FCSTD DOCUMENT  (FreeCAD 0.16RUnknown)
Label: 2d-box
License: All rights reserved
LicenseURL: http://en.wikipedia.org/wiki/All_rights_reserved
objects: Sketcher::SketchObject×6, Spreadsheet::Sheet×1
note: 6 computed .brp shape members not serialized (recipe doc carries the construction recipe); baked Part::Feature solids carry a one-line shape summary decoded from their .brp

FEATURE [Spreadsheet::Sheet] Spreadsheet  label="prefs"
  cells = A1=width; B1(width)=100; C1=mm; A2=depth; B2(depth)=50; C2=mm; A3=height; B3(height)=30; C3=mm; A4=thickness; B4(thickness)=3; C4=mm; A5=space; B5(space)=2; C5=mm
FEATURE [Sketcher::SketchObject] Sketch  label="bottom"
  expr: Constraints[50] = prefs.width - 2 * prefs.thickness
  expr: Constraints[51] = prefs.width
  expr: Constraints[21] = prefs.depth - 2 * prefs.thickness
  expr: Constraints[20] = prefs.depth - 2 * prefs.thickness
  expr: Constraints[22] = prefs.depth
  sketch-geometry (21):
    g0: LineSegment StartX=3 StartY=47 StartZ=0 EndX=34.3333 EndY=47 EndZ=0
    g1: LineSegment StartX=34.3333 StartY=47 StartZ=0 EndX=34.3333 EndY=50 EndZ=0
    g2: LineSegment StartX=34.3333 StartY=50 StartZ=0 EndX=65.6667 EndY=50 EndZ=0
    g3: LineSegment StartX=65.6667 StartY=50 StartZ=0 EndX=65.6667 EndY=47 EndZ=0
    g4: LineSegment StartX=65.6667 StartY=47 StartZ=0 EndX=97 EndY=47 EndZ=0
    g5: LineSegment StartX=97 StartY=47 StartZ=0 EndX=97 EndY=32.3333 EndZ=0
    g6: LineSegment StartX=97 StartY=32.3333 StartZ=0 EndX=100 EndY=32.3333 EndZ=0
    g7: LineSegment StartX=100 StartY=32.3333 StartZ=0 EndX=100 EndY=17.6667 EndZ=0
    g8: LineSegment StartX=100 StartY=17.6667 StartZ=0 EndX=97 EndY=17.6667 EndZ=0
    g9: LineSegment StartX=97 StartY=17.6667 StartZ=0 EndX=97 EndY=3 EndZ=0
    g10: LineSegment StartX=97 StartY=3 StartZ=0 EndX=65.6667 EndY=3 EndZ=0
    g11: LineSegment StartX=65.6667 StartY=3 StartZ=0 EndX=65.6667 EndY=0 EndZ=0
    g12: LineSegment StartX=65.6667 StartY=0 StartZ=0 EndX=34.3333 EndY=0 EndZ=0
    g13: LineSegment StartX=34.3333 StartY=0 StartZ=0 EndX=34.3333 EndY=3 EndZ=0
    g14: LineSegment StartX=34.3333 StartY=3 StartZ=0 EndX=2.99998 EndY=3 EndZ=0
    g15: LineSegment StartX=2.99998 StartY=3 StartZ=0 EndX=2.99998 EndY=17.6667 EndZ=0
    g16: LineSegment StartX=2.99998 StartY=17.6667 StartZ=0 EndX=8.10663e-07 EndY=17.6667 EndZ=0
    g17: LineSegment StartX=8.10663e-07 StartY=17.6667 StartZ=0 EndX=8.10663e-07 EndY=32.3333 EndZ=0
    g18: LineSegment StartX=8.10663e-07 StartY=32.3333 StartZ=0 EndX=3 EndY=32.3333 EndZ=0
    g19: LineSegment StartX=3 StartY=32.3333 StartZ=0 EndX=3 EndY=47 EndZ=0
    g20: GeomPoint [constr] X=-41.8758 Y=-31.3252 Z=0
  constraints (60):
    c: Coincident(g0,g1)
    c: Coincident(g1,g2)
    c: Coincident(g2,g3)
    c: Coincident(g3,g4)
    c: Coincident(g4,g5)
    c: Coincident(g5,g6)
    c: Coincident(g6,g7)
    c: Coincident(g7,g8)
    c: Coincident(g8,g9)
    c: Coincident(g9,g10)
    c: Coincident(g10,g11)
    c: Coincident(g11,g12)
    c: Coincident(g12,g13)
    c: Coincident(g13,g14)
    c: Coincident(g14,g15)
    c: Coincident(g15,g16)
    c: Coincident(g16,g17)
    c: Coincident(g17,g18)
    c: Coincident(g18,g19)
    c: Coincident(g19,g0)
    c: DistanceY(g9,g4) = 44
    c: DistanceY(g14,g0) = 44
    c: DistanceY(g12,g1) = 50
    c: Horizontal(g0)
    c: Horizontal(g2)
    c: Horizontal(g4)
    c: Horizontal(g10)
    c: Horizontal(g12)
    c: Horizontal(g14)
    c: Equal(g1,g13)
    c: Equal(g0,g2)
    c: Equal(g2,g4)
    c: Equal(g4,g10)
    c: Equal(g10,g12)
    c: Equal(g12,g14)
    c: Equal(g3,g11)
    c: Equal(g5,g7)
    c: Equal(g7,g9)
    c: Equal(g9,g19)
    c: Equal(g19,g17)
    c: Equal(g17,g15)
    c: Vertical(g3)
    c: Vertical(g1)
    c: Vertical(g13)
    c: Vertical(g11)
    c: Horizontal(g18)
    c: Horizontal(g16)
    c: Horizontal(g8)
    c: Equal(g18,g6)
    c: Equal(g16,g8)
    c: DistanceX(g0,g4) = 94
    c: DistanceX(g16,g7) = 100
    c: Vertical(g15)
    c: Vertical(g19)
    c: Vertical(g17)
    c: Vertical(g5)
    c: Vertical(g7)
    c: Vertical(g9)
    c: DistanceX(g-1,g16) = 0
    c: DistanceY(g12,g-1) = 0
FEATURE [Sketcher::SketchObject] Sketch001  label="front"
  Placement = pos=(0,52,0) rot=(0,0,1;0rad)
  expr: Placement.Base.y = prefs.depth + prefs.space
  expr: Constraints[20] = prefs.height
  expr: Constraints[21] = prefs.height
  expr: Constraints[48] = prefs.width - 2 * prefs.thickness
  expr: Constraints[49] = prefs.width
  expr: Constraints[22] = prefs.height - 2 * prefs.thickness
  sketch-geometry (21):
    g0: LineSegment StartX=3 StartY=30 StartZ=0 EndX=34.3333 EndY=30 EndZ=0
    g1: LineSegment StartX=34.3333 StartY=30 StartZ=0 EndX=34.3333 EndY=27 EndZ=0
    g2: LineSegment StartX=34.3333 StartY=27 StartZ=0 EndX=65.6667 EndY=27 EndZ=0
    g3: LineSegment StartX=65.6667 StartY=27 StartZ=0 EndX=65.6667 EndY=30 EndZ=0
    g4: LineSegment StartX=65.6667 StartY=30 StartZ=0 EndX=97 EndY=30 EndZ=0
    g5: LineSegment StartX=97 StartY=30 StartZ=0 EndX=97 EndY=20 EndZ=0
    g6: LineSegment StartX=97 StartY=20 StartZ=0 EndX=100 EndY=20 EndZ=0
    g7: LineSegment StartX=100 StartY=20 StartZ=0 EndX=100 EndY=10 EndZ=0
    g8: LineSegment StartX=100 StartY=10 StartZ=0 EndX=97 EndY=10 EndZ=0
    g9: LineSegment StartX=97 StartY=10 StartZ=0 EndX=97 EndY=0 EndZ=0
    g10: LineSegment StartX=97 StartY=0 StartZ=0 EndX=65.6667 EndY=0 EndZ=0
    g11: LineSegment StartX=65.6667 StartY=0 StartZ=0 EndX=65.6667 EndY=3 EndZ=0
    g12: LineSegment StartX=65.6667 StartY=3 StartZ=0 EndX=34.3333 EndY=3 EndZ=0
    g13: LineSegment StartX=34.3333 StartY=3 StartZ=0 EndX=34.3333 EndY=0 EndZ=0
    g14: LineSegment StartX=34.3333 StartY=0 StartZ=0 EndX=2.99998 EndY=0 EndZ=0
    g15: LineSegment StartX=2.99998 StartY=0 StartZ=0 EndX=2.99998 EndY=10 EndZ=0
    g16: LineSegment StartX=2.99998 StartY=10 StartZ=0 EndX=8.10663e-07 EndY=10 EndZ=0
    g17: LineSegment StartX=8.10663e-07 StartY=10 StartZ=0 EndX=8.10663e-07 EndY=20 EndZ=0
    g18: LineSegment StartX=8.10663e-07 StartY=20 StartZ=0 EndX=3 EndY=20 EndZ=0
    g19: LineSegment StartX=3 StartY=20 StartZ=0 EndX=3 EndY=30 EndZ=0
    g20: GeomPoint [constr] X=-41.8758 Y=-31.3252 Z=0
  constraints (60):
    c: Coincident(g0,g1)
    c: Coincident(g1,g2)
    c: Coincident(g2,g3)
    c: Coincident(g3,g4)
    c: Coincident(g4,g5)
    c: Coincident(g5,g6)
    c: Coincident(g6,g7)
    c: Coincident(g7,g8)
    c: Coincident(g8,g9)
    c: Coincident(g9,g10)
    c: Coincident(g10,g11)
    c: Coincident(g11,g12)
    c: Coincident(g12,g13)
    c: Coincident(g13,g14)
    c: Coincident(g14,g15)
    c: Coincident(g15,g16)
    c: Coincident(g16,g17)
    c: Coincident(g17,g18)
    c: Coincident(g18,g19)
    c: Coincident(g19,g0)
    c: DistanceY(g9,g4) = 30
    c: DistanceY(g14,g0) = 30
    c: DistanceY(g12,g1) = 24
    c: Horizontal(g0)
    c: Horizontal(g2)
    c: Horizontal(g4)
    c: Horizontal(g10)
    c: Horizontal(g12)
    c: Horizontal(g14)
    c: Equal(g0,g2)
    c: Equal(g2,g4)
    c: Equal(g4,g10)
    c: Equal(g10,g12)
    c: Equal(g12,g14)
    c: Equal(g5,g7)
    c: Equal(g7,g9)
    c: Equal(g9,g19)
    c: Equal(g19,g17)
    c: Equal(g17,g15)
    c: Vertical(g3)
    c: Vertical(g1)
    c: Vertical(g13)
    c: Vertical(g11)
    c: Horizontal(g18)
    c: Horizontal(g16)
    c: Horizontal(g8)
    c: Equal(g18,g6)
    c: Equal(g16,g8)
    c: DistanceX(g0,g4) = 94
    c: DistanceX(g16,g7) = 100
    c: Vertical(g15)
    c: Vertical(g19)
    c: Vertical(g17)
    c: Vertical(g5)
    c: Vertical(g7)
    c: Vertical(g9)
    c: DistanceX(g-1,g16) = 0
    c: Equal(g1,g13)
    c: Equal(g3,g11)
    c: DistanceY(g-1,g14) = 0
FEATURE [Sketcher::SketchObject] Sketch002  label="left"
  Placement = pos=(0,84,0) rot=(0,0,1;0rad)
  expr: Constraints[59] = (prefs.depth - 2 * prefs.thickness) / 3
  expr: Constraints[53] = prefs.depth - 2 * prefs.thickness
  expr: Placement.Base.y = prefs.depth + prefs.height + prefs.space * 2
  expr: Constraints[20] = prefs.height
  expr: Constraints[21] = prefs.height
  expr: Constraints[54] = prefs.depth
  expr: Constraints[22] = prefs.height - 2 * prefs.thickness
  sketch-geometry (21):
    g0: LineSegment StartX=0 StartY=30 StartZ=0 EndX=17.6667 EndY=30 EndZ=0
    g1: LineSegment StartX=17.6667 StartY=30 StartZ=0 EndX=17.6667 EndY=27 EndZ=0
    g2: LineSegment StartX=17.6667 StartY=27 StartZ=0 EndX=32.3333 EndY=27 EndZ=0
    g3: LineSegment StartX=32.3333 StartY=27 StartZ=0 EndX=32.3333 EndY=30 EndZ=0
    g4: LineSegment StartX=32.3333 StartY=30 StartZ=0 EndX=50 EndY=30 EndZ=0
    g5: LineSegment StartX=50 StartY=30 StartZ=0 EndX=50 EndY=20 EndZ=0
    g6: LineSegment StartX=50 StartY=20 StartZ=0 EndX=47 EndY=20 EndZ=0
    g7: LineSegment StartX=47 StartY=20 StartZ=0 EndX=47 EndY=10 EndZ=0
    g8: LineSegment StartX=47 StartY=10 StartZ=0 EndX=50 EndY=10 EndZ=0
    g9: LineSegment StartX=50 StartY=10 StartZ=0 EndX=50 EndY=0 EndZ=0
    g10: LineSegment StartX=50 StartY=0 StartZ=0 EndX=32.3333 EndY=0 EndZ=0
    g11: LineSegment StartX=32.3333 StartY=0 StartZ=0 EndX=32.3333 EndY=3 EndZ=0
    g12: LineSegment StartX=32.3333 StartY=3 StartZ=0 EndX=17.6667 EndY=3 EndZ=0
    g13: LineSegment StartX=17.6667 StartY=3 StartZ=0 EndX=17.6667 EndY=0 EndZ=0
    g14: LineSegment StartX=17.6667 StartY=0 StartZ=0 EndX=0 EndY=0 EndZ=0
    g15: LineSegment StartX=0 StartY=0 StartZ=0 EndX=0 EndY=10 EndZ=0
    g16: LineSegment StartX=0 StartY=10 StartZ=0 EndX=3 EndY=10 EndZ=0
    g17: LineSegment StartX=3 StartY=10 StartZ=0 EndX=3 EndY=20 EndZ=0
    g18: LineSegment StartX=3 StartY=20 StartZ=0 EndX=0 EndY=20 EndZ=0
    g19: LineSegment StartX=0 StartY=20 StartZ=0 EndX=0 EndY=30 EndZ=0
    g20: GeomPoint [constr] X=-41.8758 Y=-31.3252 Z=0
  constraints (60):
    c: Coincident(g0,g1)
    c: Coincident(g1,g2)
    c: Coincident(g2,g3)
    c: Coincident(g3,g4)
    c: Coincident(g4,g5)
    c: Coincident(g5,g6)
    c: Coincident(g6,g7)
    c: Coincident(g7,g8)
    c: Coincident(g8,g9)
    c: Coincident(g9,g10)
    c: Coincident(g10,g11)
    c: Coincident(g11,g12)
    c: Coincident(g12,g13)
    c: Coincident(g13,g14)
    c: Coincident(g14,g15)
    c: Coincident(g15,g16)
    c: Coincident(g16,g17)
    c: Coincident(g17,g18)
    c: Coincident(g18,g19)
    c: Coincident(g19,g0)
    c: DistanceY(g9,g4) = 30
    c: DistanceY(g14,g0) = 30
    c: DistanceY(g12,g1) = 24
    c: Horizontal(g0)
    c: Horizontal(g2)
    c: Horizontal(g4)
    c: Horizontal(g10)
    c: Horizontal(g12)
    c: Horizontal(g14)
    c: Equal(g4,g10)
    c: Equal(g5,g7)
    c: Equal(g7,g9)
    c: Equal(g9,g19)
    c: Equal(g19,g17)
    c: Equal(g17,g15)
    c: Vertical(g3)
    c: Vertical(g1)
    c: Vertical(g13)
    c: Vertical(g11)
    c: Horizontal(g18)
    c: Horizontal(g16)
    c: Vertical(g15)
    c: Vertical(g19)
    c: Vertical(g17)
    c: Vertical(g5)
    c: Vertical(g7)
    c: Vertical(g9)
    c: Equal(g1,g13)
    c: Equal(g3,g11)
    c: DistanceY(g-1,g14) = 0
    c: Horizontal(g6)
    c: Equal(g18,g6)
    c: Equal(g16,g8)
    c: DistanceX(g17,g6) = 44
    c: DistanceX(g0,g4) = 50
    c: DistanceX(g-1,g14) = 0
    c: Equal(g14,g10)
    c: Equal(g0,g4)
    c: Equal(g2,g12)
    c: DistanceX(g2,g2) = 14.6667
FEATURE [Sketcher::SketchObject] Sketch003  label="top"
  Placement = pos=(102,0,0) rot=(0,0,1;0rad)
  expr: Placement.Base.x = prefs.width + prefs.space
  expr: Constraints[50] = prefs.width - 2 * prefs.thickness
  expr: Constraints[51] = prefs.width
  expr: Constraints[21] = prefs.depth - 2 * prefs.thickness
  expr: Constraints[20] = prefs.depth - 2 * prefs.thickness
  expr: Constraints[22] = prefs.depth
  sketch-geometry (21):
    g0: LineSegment StartX=3 StartY=47 StartZ=0 EndX=34.3333 EndY=47 EndZ=0
    g1: LineSegment StartX=34.3333 StartY=47 StartZ=0 EndX=34.3333 EndY=50 EndZ=0
    g2: LineSegment StartX=34.3333 StartY=50 StartZ=0 EndX=65.6667 EndY=50 EndZ=0
    g3: LineSegment StartX=65.6667 StartY=50 StartZ=0 EndX=65.6667 EndY=47 EndZ=0
    g4: LineSegment StartX=65.6667 StartY=47 StartZ=0 EndX=97 EndY=47 EndZ=0
    g5: LineSegment StartX=97 StartY=47 StartZ=0 EndX=97 EndY=32.3333 EndZ=0
    g6: LineSegment StartX=97 StartY=32.3333 StartZ=0 EndX=100 EndY=32.3333 EndZ=0
    g7: LineSegment StartX=100 StartY=32.3333 StartZ=0 EndX=100 EndY=17.6667 EndZ=0
    g8: LineSegment StartX=100 StartY=17.6667 StartZ=0 EndX=97 EndY=17.6667 EndZ=0
    g9: LineSegment StartX=97 StartY=17.6667 StartZ=0 EndX=97 EndY=3 EndZ=0
    g10: LineSegment StartX=97 StartY=3 StartZ=0 EndX=65.6667 EndY=3 EndZ=0
    g11: LineSegment StartX=65.6667 StartY=3 StartZ=0 EndX=65.6667 EndY=0 EndZ=0
    g12: LineSegment StartX=65.6667 StartY=0 StartZ=0 EndX=34.3333 EndY=0 EndZ=0
    g13: LineSegment StartX=34.3333 StartY=0 StartZ=0 EndX=34.3333 EndY=3 EndZ=0
    g14: LineSegment StartX=34.3333 StartY=3 StartZ=0 EndX=2.99998 EndY=3 EndZ=0
    g15: LineSegment StartX=2.99998 StartY=3 StartZ=0 EndX=2.99998 EndY=17.6667 EndZ=0
    g16: LineSegment StartX=2.99998 StartY=17.6667 StartZ=0 EndX=8.10663e-07 EndY=17.6667 EndZ=0
    g17: LineSegment StartX=8.10663e-07 StartY=17.6667 StartZ=0 EndX=8.10663e-07 EndY=32.3333 EndZ=0
    g18: LineSegment StartX=8.10663e-07 StartY=32.3333 StartZ=0 EndX=3 EndY=32.3333 EndZ=0
    g19: LineSegment StartX=3 StartY=32.3333 StartZ=0 EndX=3 EndY=47 EndZ=0
    g20: GeomPoint [constr] X=-41.8758 Y=-31.3252 Z=0
  constraints (60):
    c: Coincident(g0,g1)
    c: Coincident(g1,g2)
    c: Coincident(g2,g3)
    c: Coincident(g3,g4)
    c: Coincident(g4,g5)
    c: Coincident(g5,g6)
    c: Coincident(g6,g7)
    c: Coincident(g7,g8)
    c: Coincident(g8,g9)
    c: Coincident(g9,g10)
    c: Coincident(g10,g11)
    c: Coincident(g11,g12)
    c: Coincident(g12,g13)
    c: Coincident(g13,g14)
    c: Coincident(g14,g15)
    c: Coincident(g15,g16)
    c: Coincident(g16,g17)
    c: Coincident(g17,g18)
    c: Coincident(g18,g19)
    c: Coincident(g19,g0)
    c: DistanceY(g9,g4) = 44
    c: DistanceY(g14,g0) = 44
    c: DistanceY(g12,g1) = 50
    c: Horizontal(g0)
    c: Horizontal(g2)
    c: Horizontal(g4)
    c: Horizontal(g10)
    c: Horizontal(g12)
    c: Horizontal(g14)
    c: Equal(g1,g13)
    c: Equal(g0,g2)
    c: Equal(g2,g4)
    c: Equal(g4,g10)
    c: Equal(g10,g12)
    c: Equal(g12,g14)
    c: Equal(g3,g11)
    c: Equal(g5,g7)
    c: Equal(g7,g9)
    c: Equal(g9,g19)
    c: Equal(g19,g17)
    c: Equal(g17,g15)
    c: Vertical(g3)
    c: Vertical(g1)
    c: Vertical(g13)
    c: Vertical(g11)
    c: Horizontal(g18)
    c: Horizontal(g16)
    c: Horizontal(g8)
    c: Equal(g18,g6)
    c: Equal(g16,g8)
    c: DistanceX(g0,g4) = 94
    c: DistanceX(g16,g7) = 100
    c: Vertical(g15)
    c: Vertical(g19)
    c: Vertical(g17)
    c: Vertical(g5)
    c: Vertical(g7)
    c: Vertical(g9)
    c: DistanceX(g-1,g16) = 0
    c: DistanceY(g12,g-1) = 0
FEATURE [Sketcher::SketchObject] Sketch004  label="back"
  Placement = pos=(102,52,0) rot=(0,0,1;0rad)
  expr: Placement.Base.x = prefs.width + prefs.space
  expr: Placement.Base.y = prefs.depth + prefs.space
  expr: Constraints[20] = prefs.height
  expr: Constraints[21] = prefs.height
  expr: Constraints[48] = prefs.width - 2 * prefs.thickness
  expr: Constraints[49] = prefs.width
  expr: Constraints[22] = prefs.height - 2 * prefs.thickness
  sketch-geometry (21):
    g0: LineSegment StartX=3 StartY=30 StartZ=0 EndX=34.3333 EndY=30 EndZ=0
    g1: LineSegment StartX=34.3333 StartY=30 StartZ=0 EndX=34.3333 EndY=27 EndZ=0
    g2: LineSegment StartX=34.3333 StartY=27 StartZ=0 EndX=65.6667 EndY=27 EndZ=0
    g3: LineSegment StartX=65.6667 StartY=27 StartZ=0 EndX=65.6667 EndY=30 EndZ=0
    g4: LineSegment StartX=65.6667 StartY=30 StartZ=0 EndX=97 EndY=30 EndZ=0
    g5: LineSegment StartX=97 StartY=30 StartZ=0 EndX=97 EndY=20 EndZ=0
    g6: LineSegment StartX=97 StartY=20 StartZ=0 EndX=100 EndY=20 EndZ=0
    g7: LineSegment StartX=100 StartY=20 StartZ=0 EndX=100 EndY=10 EndZ=0
    g8: LineSegment StartX=100 StartY=10 StartZ=0 EndX=97 EndY=10 EndZ=0
    g9: LineSegment StartX=97 StartY=10 StartZ=0 EndX=97 EndY=0 EndZ=0
    g10: LineSegment StartX=97 StartY=0 StartZ=0 EndX=65.6667 EndY=0 EndZ=0
    g11: LineSegment StartX=65.6667 StartY=0 StartZ=0 EndX=65.6667 EndY=3 EndZ=0
    g12: LineSegment StartX=65.6667 StartY=3 StartZ=0 EndX=34.3333 EndY=3 EndZ=0
    g13: LineSegment StartX=34.3333 StartY=3 StartZ=0 EndX=34.3333 EndY=0 EndZ=0
    g14: LineSegment StartX=34.3333 StartY=0 StartZ=0 EndX=2.99998 EndY=0 EndZ=0
    g15: LineSegment StartX=2.99998 StartY=0 StartZ=0 EndX=2.99998 EndY=10 EndZ=0
    g16: LineSegment StartX=2.99998 StartY=10 StartZ=0 EndX=8.10663e-07 EndY=10 EndZ=0
    g17: LineSegment StartX=8.10663e-07 StartY=10 StartZ=0 EndX=8.10663e-07 EndY=20 EndZ=0
    g18: LineSegment StartX=8.10663e-07 StartY=20 StartZ=0 EndX=3 EndY=20 EndZ=0
    g19: LineSegment StartX=3 StartY=20 StartZ=0 EndX=3 EndY=30 EndZ=0
    g20: GeomPoint [constr] X=-41.8758 Y=-31.3252 Z=0
  constraints (60):
    c: Coincident(g0,g1)
    c: Coincident(g1,g2)
    c: Coincident(g2,g3)
    c: Coincident(g3,g4)
    c: Coincident(g4,g5)
    c: Coincident(g5,g6)
    c: Coincident(g6,g7)
    c: Coincident(g7,g8)
    c: Coincident(g8,g9)
    c: Coincident(g9,g10)
    c: Coincident(g10,g11)
    c: Coincident(g11,g12)
    c: Coincident(g12,g13)
    c: Coincident(g13,g14)
    c: Coincident(g14,g15)
    c: Coincident(g15,g16)
    c: Coincident(g16,g17)
    c: Coincident(g17,g18)
    c: Coincident(g18,g19)
    c: Coincident(g19,g0)
    c: DistanceY(g9,g4) = 30
    c: DistanceY(g14,g0) = 30
    c: DistanceY(g12,g1) = 24
    c: Horizontal(g0)
    c: Horizontal(g2)
    c: Horizontal(g4)
    c: Horizontal(g10)
    c: Horizontal(g12)
    c: Horizontal(g14)
    c: Equal(g0,g2)
    c: Equal(g2,g4)
    c: Equal(g4,g10)
    c: Equal(g10,g12)
    c: Equal(g12,g14)
    c: Equal(g5,g7)
    c: Equal(g7,g9)
    c: Equal(g9,g19)
    c: Equal(g19,g17)
    c: Equal(g17,g15)
    c: Vertical(g3)
    c: Vertical(g1)
    c: Vertical(g13)
    c: Vertical(g11)
    c: Horizontal(g18)
    c: Horizontal(g16)
    c: Horizontal(g8)
    c: Equal(g18,g6)
    c: Equal(g16,g8)
    c: DistanceX(g0,g4) = 94
    c: DistanceX(g16,g7) = 100
    c: Vertical(g15)
    c: Vertical(g19)
    c: Vertical(g17)
    c: Vertical(g5)
    c: Vertical(g7)
    c: Vertical(g9)
    c: DistanceX(g-1,g16) = 0
    c: Equal(g1,g13)
    c: Equal(g3,g11)
    c: DistanceY(g-1,g14) = 0
FEATURE [Sketcher::SketchObject] Sketch006  label="right"
  Placement = pos=(52,84,0) rot=(0,0,1;0rad)
  expr: Placement.Base.x = prefs.depth + prefs.space
  expr: Constraints[59] = (prefs.depth - 2 * prefs.thickness) / 3
  expr: Constraints[53] = prefs.depth - 2 * prefs.thickness
  expr: Placement.Base.y = prefs.depth + prefs.height + prefs.space * 2
  expr: Constraints[20] = prefs.height
  expr: Constraints[21] = prefs.height
  expr: Constraints[54] = prefs.depth
  expr: Constraints[22] = prefs.height - 2 * prefs.thickness
  sketch-geometry (21):
    g0: LineSegment StartX=0 StartY=30 StartZ=0 EndX=17.6667 EndY=30 EndZ=0
    g1: LineSegment StartX=17.6667 StartY=30 StartZ=0 EndX=17.6667 EndY=27 EndZ=0
    g2: LineSegment StartX=17.6667 StartY=27 StartZ=0 EndX=32.3333 EndY=27 EndZ=0
    g3: LineSegment StartX=32.3333 StartY=27 StartZ=0 EndX=32.3333 EndY=30 EndZ=0
    g4: LineSegment StartX=32.3333 StartY=30 StartZ=0 EndX=50 EndY=30 EndZ=0
    g5: LineSegment StartX=50 StartY=30 StartZ=0 EndX=50 EndY=20 EndZ=0
    g6: LineSegment StartX=50 StartY=20 StartZ=0 EndX=47 EndY=20 EndZ=0
    g7: LineSegment StartX=47 StartY=20 StartZ=0 EndX=47 EndY=10 EndZ=0
    g8: LineSegment StartX=47 StartY=10 StartZ=0 EndX=50 EndY=10 EndZ=0
    g9: LineSegment StartX=50 StartY=10 StartZ=0 EndX=50 EndY=0 EndZ=0
    g10: LineSegment StartX=50 StartY=0 StartZ=0 EndX=32.3333 EndY=0 EndZ=0
    g11: LineSegment StartX=32.3333 StartY=0 StartZ=0 EndX=32.3333 EndY=3 EndZ=0
    g12: LineSegment StartX=32.3333 StartY=3 StartZ=0 EndX=17.6667 EndY=3 EndZ=0
    g13: LineSegment StartX=17.6667 StartY=3 StartZ=0 EndX=17.6667 EndY=0 EndZ=0
    g14: LineSegment StartX=17.6667 StartY=0 StartZ=0 EndX=0 EndY=0 EndZ=0
    g15: LineSegment StartX=0 StartY=0 StartZ=0 EndX=0 EndY=10 EndZ=0
    g16: LineSegment StartX=0 StartY=10 StartZ=0 EndX=3 EndY=10 EndZ=0
    g17: LineSegment StartX=3 StartY=10 StartZ=0 EndX=3 EndY=20 EndZ=0
    g18: LineSegment StartX=3 StartY=20 StartZ=0 EndX=0 EndY=20 EndZ=0
    g19: LineSegment StartX=0 StartY=20 StartZ=0 EndX=0 EndY=30 EndZ=0
    g20: GeomPoint [constr] X=-41.8758 Y=-31.3252 Z=0
  constraints (60):
    c: Coincident(g0,g1)
    c: Coincident(g1,g2)
    c: Coincident(g2,g3)
    c: Coincident(g3,g4)
    c: Coincident(g4,g5)
    c: Coincident(g5,g6)
    c: Coincident(g6,g7)
    c: Coincident(g7,g8)
    c: Coincident(g8,g9)
    c: Coincident(g9,g10)
    c: Coincident(g10,g11)
    c: Coincident(g11,g12)
    c: Coincident(g12,g13)
    c: Coincident(g13,g14)
    c: Coincident(g14,g15)
    c: Coincident(g15,g16)
    c: Coincident(g16,g17)
    c: Coincident(g17,g18)
    c: Coincident(g18,g19)
    c: Coincident(g19,g0)
    c: DistanceY(g9,g4) = 30
    c: DistanceY(g14,g0) = 30
    c: DistanceY(g12,g1) = 24
    c: Horizontal(g0)
    c: Horizontal(g2)
    c: Horizontal(g4)
    c: Horizontal(g10)
    c: Horizontal(g12)
    c: Horizontal(g14)
    c: Equal(g4,g10)
    c: Equal(g5,g7)
    c: Equal(g7,g9)
    c: Equal(g9,g19)
    c: Equal(g19,g17)
    c: Equal(g17,g15)
    c: Vertical(g3)
    c: Vertical(g1)
    c: Vertical(g13)
    c: Vertical(g11)
    c: Horizontal(g18)
    c: Horizontal(g16)
    c: Vertical(g15)
    c: Vertical(g19)
    c: Vertical(g17)
    c: Vertical(g5)
    c: Vertical(g7)
    c: Vertical(g9)
    c: Equal(g1,g13)
    c: Equal(g3,g11)
    c: DistanceY(g-1,g14) = 0
    c: Horizontal(g6)
    c: Equal(g18,g6)
    c: Equal(g16,g8)
    c: DistanceX(g17,g6) = 44
    c: DistanceX(g0,g4) = 50
    c: DistanceX(g-1,g14) = 0
    c: Equal(g14,g10)
    c: Equal(g0,g4)
    c: Equal(g2,g12)
    c: DistanceX(g2,g2) = 14.6667
